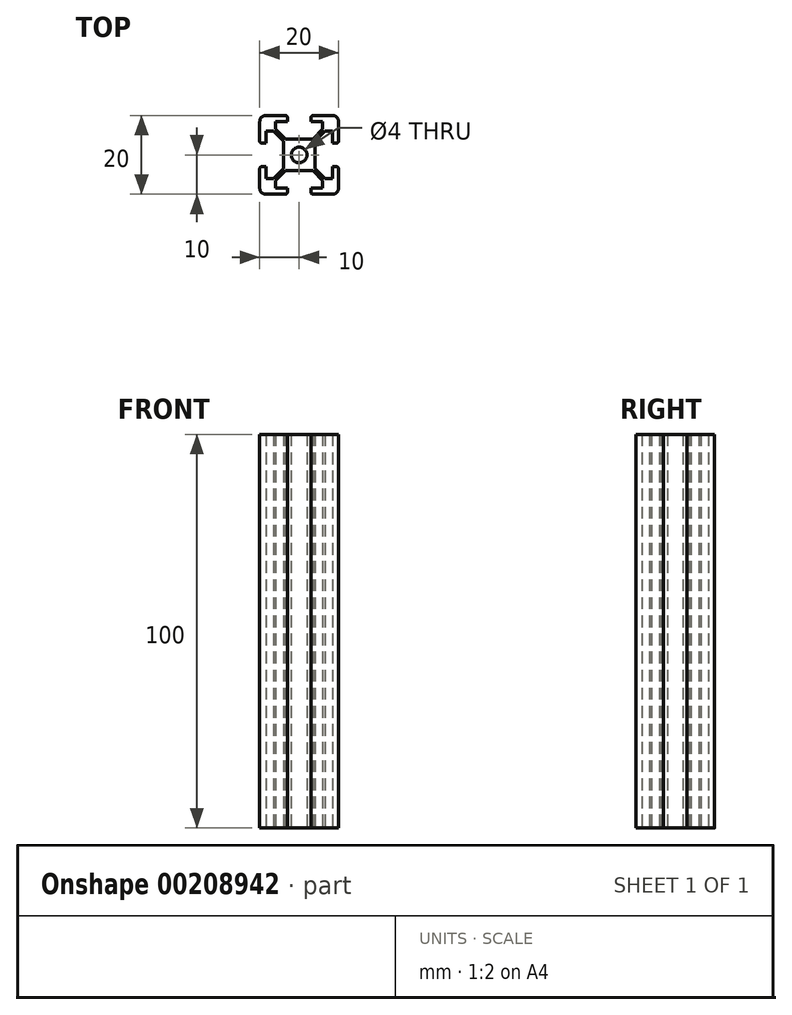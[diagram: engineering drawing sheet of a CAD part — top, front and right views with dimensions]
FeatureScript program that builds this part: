
annotation { "Feature Type Name" : "Feature", "Feature Type Description" : "" }
export const myFeature = defineFeature(function(context is Context, id is Id, definition is map)
    precondition{}
    {
        {
            var Q0;
            Q0=qCreatedBy(makeId("Top.planeOp"),FACE);
            var sketch = newSketch(context, id + "F0", { "sketchPlane" : qUnion([Q0])});
            skCircle(sketch, "E0", {"center": v(0, 0) * mm, "radius": 2 * mm});
            skLineSegment(sketch, "E1", {"start": v(9.5, 3) * mm, "end": v(8.46, 3) * mm});
            skLineSegment(sketch, "E2", {"start": v(8.46, 3) * mm, "end": v(8.46, 6) * mm});
            skLineSegment(sketch, "E3", {"start": v(8.46, 6) * mm, "end": v(6.51, 6) * mm});
            skLineSegment(sketch, "E4", {"start": v(6.51, 6) * mm, "end": v(4, 3.49) * mm});
            skLineSegment(sketch, "E5", {"start": v(4, 3.49) * mm, "end": v(4, 0) * mm});
            skLineSegment(sketch, "E6", {"start": v(10, 8.5) * mm, "end": v(10, 3.5) * mm});
            skLineSegment(sketch, "E7.MirrorCS", {"start": v(3, 9.5) * mm, "end": v(3, 8.46) * mm});
            skLineSegment(sketch, "E8.MirrorCS", {"start": v(8.5, 10) * mm, "end": v(3.5, 10) * mm});
            skLineSegment(sketch, "E9.MirrorCS", {"start": v(3, 8.46) * mm, "end": v(6, 8.46) * mm});
            skLineSegment(sketch, "E10.MirrorCS", {"start": v(6, 6.51) * mm, "end": v(3.49, 4) * mm});
            skLineSegment(sketch, "E11.MirrorCS", {"start": v(3.49, 4) * mm, "end": v(0, 4) * mm});
            skLineSegment(sketch, "E12", {"start": v(6, 8.46) * mm, "end": v(6, 6.51) * mm});
            skPoint(sketch, "E13.visualSharp", {"position": v(10, 10) * mm});
            skArc(sketch, "E13.filletArc", {"start": v(10, 8.5) * mm, "mid": v(9.56, 9.56) * mm, "end": v(8.5, 10) * mm});
            skPoint(sketch, "E14.visualSharp", {"position": v(10, 3) * mm});
            skArc(sketch, "E14.filletArc", {"start": v(9.5, 3) * mm, "mid": v(9.85, 3.15) * mm, "end": v(10, 3.5) * mm});
            skPoint(sketch, "E15.visualSharp", {"position": v(3, 10) * mm});
            skArc(sketch, "E15.filletArc", {"start": v(3.5, 10) * mm, "mid": v(3.15, 9.85) * mm, "end": v(3, 9.5) * mm});
            skLineSegment(sketch, "E16.MirrorCS", {"start": v(-9.5, 3) * mm, "end": v(-8.46, 3) * mm});
            skLineSegment(sketch, "E17.MirrorCS", {"start": v(-8.46, 3) * mm, "end": v(-8.46, 6) * mm});
            skLineSegment(sketch, "E18.MirrorCS", {"start": v(-8.46, 6) * mm, "end": v(-6.51, 6) * mm});
            skLineSegment(sketch, "E19.MirrorCS", {"start": v(-6.51, 6) * mm, "end": v(-4, 3.49) * mm});
            skLineSegment(sketch, "E20.MirrorCS", {"start": v(-10, 8.5) * mm, "end": v(-10, 3.5) * mm});
            skPoint(sketch, "E21.MirrorP", {"position": v(-3, 10) * mm});
            skArc(sketch, "E22.MirrorCS", {"start": v(-10, 8.5) * mm, "mid": v(-9.56, 9.56) * mm, "end": v(-8.5, 10) * mm});
            skArc(sketch, "E23.MirrorCS", {"start": v(-9.5, 3) * mm, "mid": v(-9.85, 3.15) * mm, "end": v(-10, 3.5) * mm});
            skPoint(sketch, "E24.MirrorP", {"position": v(-10, 3) * mm});
            skPoint(sketch, "E25.MirrorP", {"position": v(-10, 10) * mm});
            skLineSegment(sketch, "E26.MirrorCS", {"start": v(-6, 6.51) * mm, "end": v(-3.49, 4) * mm});
            skLineSegment(sketch, "E27.MirrorCS", {"start": v(-3, 9.5) * mm, "end": v(-3, 8.46) * mm});
            skArc(sketch, "E28.MirrorCS", {"start": v(-3.5, 10) * mm, "mid": v(-3.15, 9.85) * mm, "end": v(-3, 9.5) * mm});
            skLineSegment(sketch, "E29.MirrorCS", {"start": v(-3, 8.46) * mm, "end": v(-6, 8.46) * mm});
            skLineSegment(sketch, "E30.MirrorCS", {"start": v(-6, 8.46) * mm, "end": v(-6, 6.51) * mm});
            skLineSegment(sketch, "E31.MirrorCS", {"start": v(-3.49, 4) * mm, "end": v(0, 4) * mm});
            skLineSegment(sketch, "E32.MirrorCS", {"start": v(-8.5, 10) * mm, "end": v(-3.5, 10) * mm});
            skLineSegment(sketch, "E33.MirrorCS", {"start": v(-4, 3.49) * mm, "end": v(-4, 0) * mm});
            skArc(sketch, "E34.MirrorCS", {"start": v(10, -8.5) * mm, "mid": v(9.56, -9.56) * mm, "end": v(8.5, -10) * mm});
            skLineSegment(sketch, "E35.MirrorCS", {"start": v(8.46, -6) * mm, "end": v(6.51, -6) * mm});
            skArc(sketch, "E36.MirrorCS", {"start": v(3.5, -10) * mm, "mid": v(3.15, -9.85) * mm, "end": v(3, -9.5) * mm});
            skLineSegment(sketch, "E37.MirrorCS", {"start": v(-3.49, -4) * mm, "end": v(0, -4) * mm});
            skLineSegment(sketch, "E38.MirrorCS", {"start": v(-3, -9.5) * mm, "end": v(-3, -8.46) * mm});
            skLineSegment(sketch, "E39.MirrorCS", {"start": v(8.5, -10) * mm, "end": v(3.5, -10) * mm});
            skLineSegment(sketch, "E40.MirrorCS", {"start": v(-3, -8.46) * mm, "end": v(-6, -8.46) * mm});
            skArc(sketch, "E41.MirrorCS", {"start": v(-10, -8.5) * mm, "mid": v(-9.56, -9.56) * mm, "end": v(-8.5, -10) * mm});
            skLineSegment(sketch, "E42.MirrorCS", {"start": v(3, -9.5) * mm, "end": v(3, -8.46) * mm});
            skLineSegment(sketch, "E43.MirrorCS", {"start": v(3, -8.46) * mm, "end": v(6, -8.46) * mm});
            skLineSegment(sketch, "E44.MirrorCS", {"start": v(3.49, -4) * mm, "end": v(0, -4) * mm});
            skLineSegment(sketch, "E45.MirrorCS", {"start": v(6, -6.51) * mm, "end": v(3.49, -4) * mm});
            skPoint(sketch, "E46.MirrorP", {"position": v(-3, -10) * mm});
            skPoint(sketch, "E47.MirrorP", {"position": v(3, -10) * mm});
            skPoint(sketch, "E48.MirrorP", {"position": v(10, -10) * mm});
            skLineSegment(sketch, "E49.MirrorCS", {"start": v(-6, -8.46) * mm, "end": v(-6, -6.51) * mm});
            skLineSegment(sketch, "E50.MirrorCS", {"start": v(6, -8.46) * mm, "end": v(6, -6.51) * mm});
            skArc(sketch, "E51.MirrorCS", {"start": v(-3.5, -10) * mm, "mid": v(-3.15, -9.85) * mm, "end": v(-3, -9.5) * mm});
            skPoint(sketch, "E52.MirrorP", {"position": v(-10, -10) * mm});
            skLineSegment(sketch, "E53.MirrorCS", {"start": v(-8.5, -10) * mm, "end": v(-3.5, -10) * mm});
            skLineSegment(sketch, "E54.MirrorCS", {"start": v(-8.46, -6) * mm, "end": v(-6.51, -6) * mm});
            skLineSegment(sketch, "E55.MirrorCS", {"start": v(-6, -6.51) * mm, "end": v(-3.49, -4) * mm});
            skLineSegment(sketch, "E56.MirrorCS", {"start": v(-10, -8.5) * mm, "end": v(-10, -3.5) * mm});
            skLineSegment(sketch, "E57.MirrorCS", {"start": v(-8.46, -3) * mm, "end": v(-8.46, -6) * mm});
            skLineSegment(sketch, "E58.MirrorCS", {"start": v(-6.51, -6) * mm, "end": v(-4, -3.49) * mm});
            skLineSegment(sketch, "E59.MirrorCS", {"start": v(-4, -3.49) * mm, "end": v(-4, 0) * mm});
            skArc(sketch, "E60.MirrorCS", {"start": v(-9.5, -3) * mm, "mid": v(-9.85, -3.15) * mm, "end": v(-10, -3.5) * mm});
            skLineSegment(sketch, "E61.MirrorCS", {"start": v(-9.5, -3) * mm, "end": v(-8.46, -3) * mm});
            skPoint(sketch, "E62.MirrorP", {"position": v(-10, -3) * mm});
            skLineSegment(sketch, "E63.MirrorCS", {"start": v(8.46, -3) * mm, "end": v(8.46, -6) * mm});
            skLineSegment(sketch, "E64.MirrorCS", {"start": v(9.5, -3) * mm, "end": v(8.46, -3) * mm});
            skArc(sketch, "E65.MirrorCS", {"start": v(9.5, -3) * mm, "mid": v(9.85, -3.15) * mm, "end": v(10, -3.5) * mm});
            skLineSegment(sketch, "E66.MirrorCS", {"start": v(6.51, -6) * mm, "end": v(4, -3.49) * mm});
            skPoint(sketch, "E67.MirrorP", {"position": v(10, -3) * mm});
            skLineSegment(sketch, "E68.MirrorCS", {"start": v(4, -3.49) * mm, "end": v(4, 0) * mm});
            skLineSegment(sketch, "E69.MirrorCS", {"start": v(10, -8.5) * mm, "end": v(10, -3.5) * mm});
            skSolve(sketch);
        }
        {
            var Q0;
            Q0=makeQuery(id+"F0.imprint","IMPRINT",FACE,{"disambiguationData":[TD([[makeQuery(id+"F0.imprint","IMPRINT",EDGE,{"derivedFrom":sQuery(id+"F0.wireOp",EDGE,"E0")}),-1.0]])]});
            extrude(context, id + "F1", {"entities" : qUnion([Q0]), "depth" : 100 * mm});
        }
    });
